# Revit family: Toilet-Round_Front-American_Standard-Cadet-3376128ST.020
name_source: partatom
category: Plumbing Fixtures
units: mm (PartAtom-declared; Revit-internal decimal feet)

## family parameters
Always vertical = No
Cut with Voids When Loaded = No
OmniClass Number = 23.45.05.21.11.11
OmniClass Title = Water Operated Water Closets
Part Type = Normal
Room Calculation Point = No
Round Connector Dimension = Use Diameter
Shared = Yes
Work Plane-Based = Yes

## types (1)
- 3376128ST.020
    ADA Compliant = Yes
    ASME A112.19.2M for Vitreous China Fixtures = Yes
    Assembly Code = D2010110
    CEC Compliant = Yes
    CW Connection = Yes
    CWFU = 10
    CalGreen Compliant = Yes
    Cold Water Connection Diameter = 3/8"
    Cold Water Connection Height = 8"
    Cold Water Connection Width = 6"
    Default Elevation = 0"
    Description = Cadet 3 FloWise 1.28 GPF/4.8 LPF Left Trip Lever 16/1-2-in. Round-Front Toilet with Slow-Close Seat
    EPA WaterSense® Certified = Yes
    Finish = Vitreous China-American Standard-020-White
    Finish - Trip Lever = Metal-American Standard-Chrome
    Flush Rate = 1.28 GPF/4.8 LPF
    HW Connection = No
    HWFU = 0
    Height = 30 3/8"
    Installation Instruction Link = https://americanstandard.box.com
    Installation Type = Floor Mounted
    Length = 26 1/4"
    Manufacturer = American Standard
    Material = Vitreous China-American Standard-020-White
    Model = 3376128ST.020
    Price = Prices may vary. Please consult Manufacturer Representative for most up-to-date price list.
    Product Documentation Link = https://americanstandard.box.com
    Product Page URL = https://www.americanstandard.ca
    Revised Date = 10/18/2022
    URL = https://www.americanstandard.ca
    Vent Connection = No
    WFU = 10
    Warranty Information = Limited Lifetime Warranty on Chinaware; 5-Year Warranty on Mechanical Parts; 1-Year Warranty on Seat
    Waste Connection = Yes
    Waste Connection Diameter = 2 1/8"
    Width = 17 1/4"

## geometry (parser evidence)
native form markers: Sweep x2
no freeform markers — native parametric forms only
